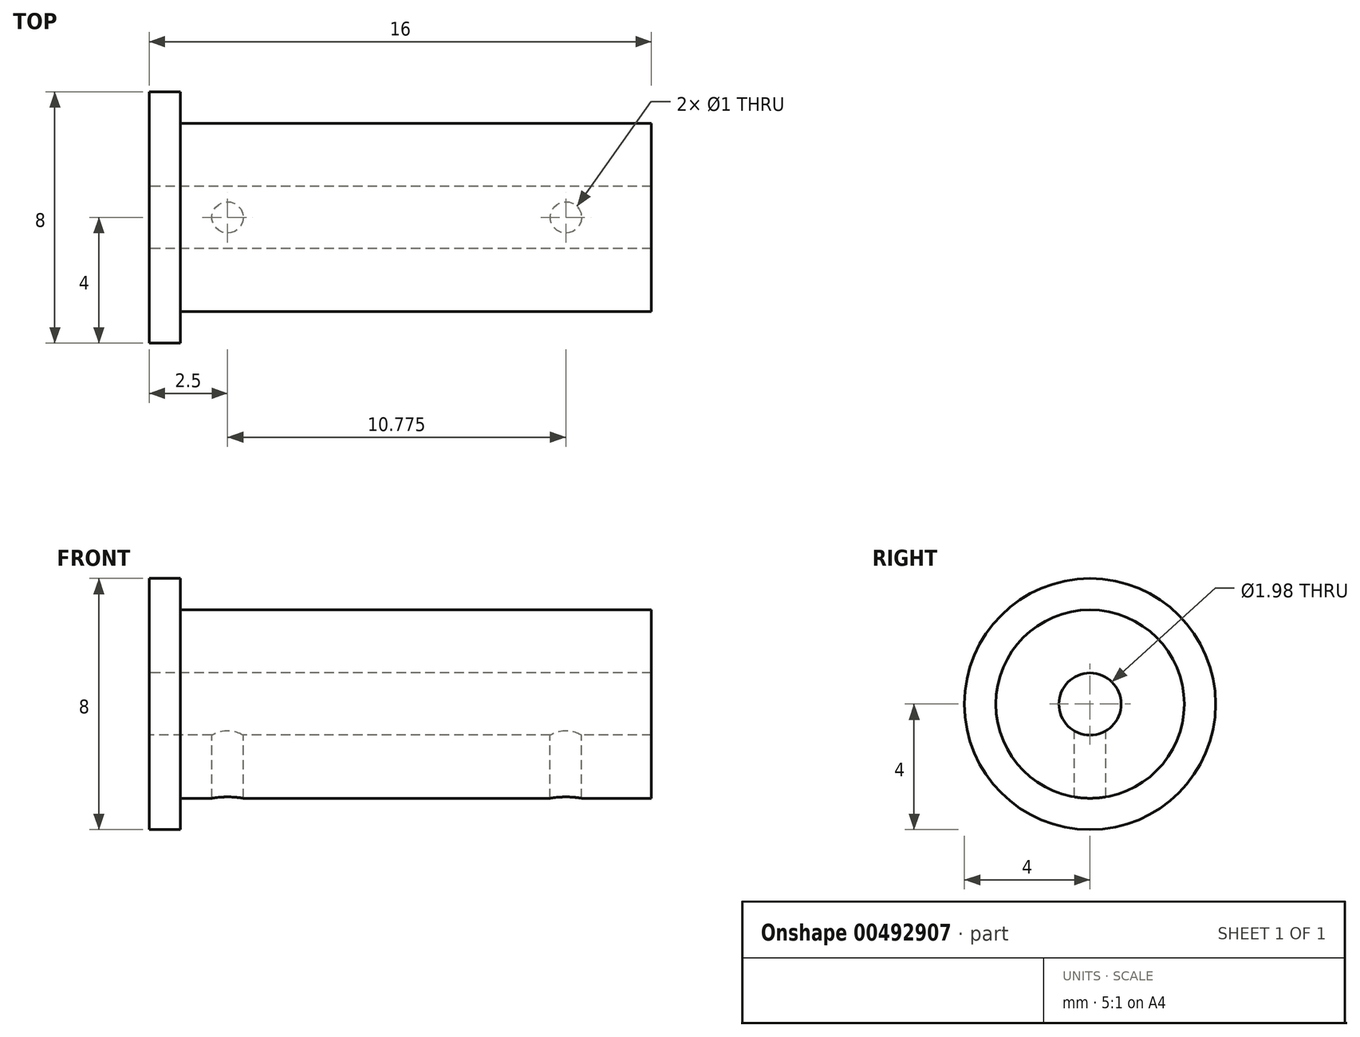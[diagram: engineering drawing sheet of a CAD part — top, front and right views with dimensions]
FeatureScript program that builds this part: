
annotation { "Feature Type Name" : "Feature", "Feature Type Description" : "" }
export const myFeature = defineFeature(function(context is Context, id is Id, definition is map)
    precondition{}
    {
        {
            var Q0;
            Q0=qCreatedBy(makeId("Front.planeOp"),FACE);
            var sketch = newSketch(context, id + "F0", { "sketchPlane" : qUnion([Q0])});
            skLineSegment(sketch, "E0", {"start": v(-47.68, 0) * mm, "end": v(45.36, 0) * mm, "construction": true});
            skLineSegment(sketch, "E1", {"start": v(0, 0) * mm, "end": v(0, 4) * mm});
            skLineSegment(sketch, "E2", {"start": v(16, 3) * mm, "end": v(16, 0) * mm});
            skLineSegment(sketch, "E3", {"start": v(16, 3) * mm, "end": v(1, 3) * mm});
            skLineSegment(sketch, "E4", {"start": v(1, 3) * mm, "end": v(1, 4) * mm});
            skLineSegment(sketch, "E5", {"start": v(1, 4) * mm, "end": v(0, 4) * mm});
            skLineSegment(sketch, "E6", {"start": v(0, 0.99) * mm, "end": v(16, 0.99) * mm});
            skSolve(sketch);
        }
        {
            var Q0;
            Q0=makeQuery(id+"F0.imprint","IMPRINT",FACE,{"disambiguationData":[TD([[makeQuery(id+"F0.imprint","IMPRINT",EDGE,{"derivedFrom":sQuery(id+"F0.wireOp",EDGE,"REZSE4bB-1knZ-V183-olf2-UWpIJi66LKXE")}),-1.0]])]});
            var Q1;
            {var subQ0=sQuery(id+"F0.wireOp",EDGE,"E3");Q1=makeQuery(id+"F0.imprint","IMPRINT",FACE,{"disambiguationData":[TD([[makeQuery(id+"F0.imprint","IMPRINT",EDGE,{"derivedFrom":subQ0}),1.0]])]});}
            var Q2;
            Q2=sQuery(id+"F0.wireOp",EDGE,"E0");
            revolve(context, id + "F1", {"entities" : qUnion([Q0, Q1]), "axis" : qUnion([Q2]), "revolveType" : RevolveType.FULL});
        }
        {
            var Q0;
            Q0=qCreatedBy(makeId("Top.planeOp"),FACE);
            var sketch = newSketch(context, id + "F2", { "sketchPlane" : qUnion([Q0])});
            skCircle(sketch, "E7", {"center": v(2.5, 0) * mm, "radius": 0.5 * mm});
            skLineSegment(sketch, "E8", {"start": v(0, 0) * mm, "end": v(7.15, 0) * mm, "construction": true});
            skCircle(sketch, "E9", {"center": v(13.28, 0) * mm, "radius": 0.5 * mm});
            skSolve(sketch);
        }
        {
            var Q0;
            Q0=qSketchRegion(id+"F2",true);
            extrude(context, id + "F3", {"entities" : qUnion([Q0]), "operationType" : NewBodyOperationType.REMOVE, "endBound" : BoundingType.THROUGH_ALL, "oppositeDirection" : true, "depth" : 25 * mm});
        }
    });
